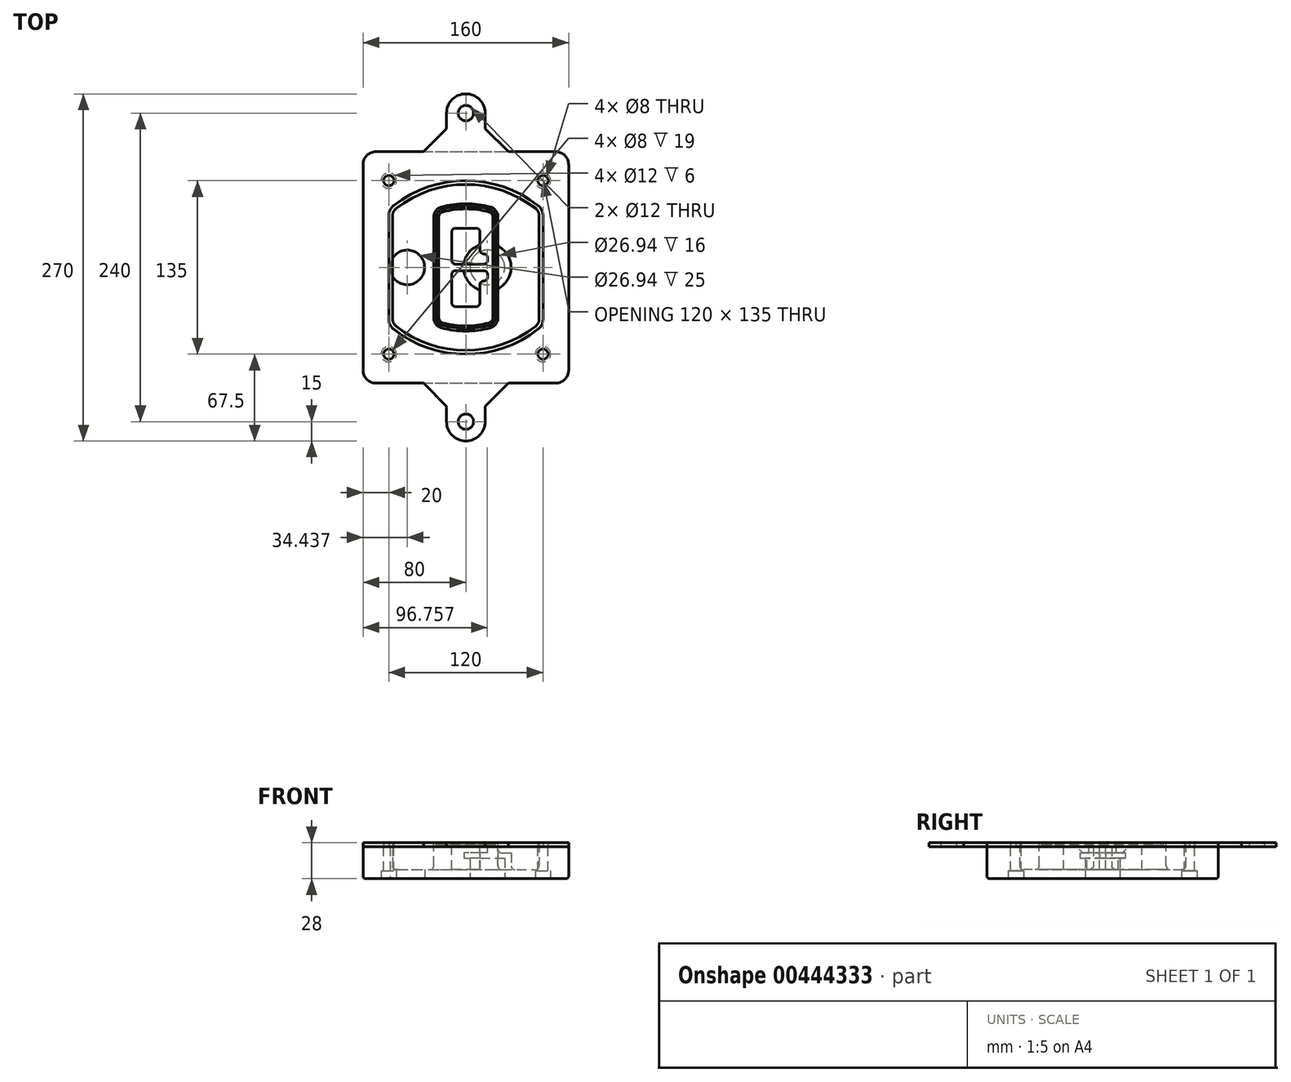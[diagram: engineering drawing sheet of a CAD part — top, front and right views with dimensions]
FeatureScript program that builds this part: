
annotation { "Feature Type Name" : "Feature", "Feature Type Description" : "" }
export const myFeature = defineFeature(function(context is Context, id is Id, definition is map)
    precondition{}
    {
        {
            var Q0;
            Q0=qCreatedBy(makeId("Top.planeOp"),FACE);
            var sketch = newSketch(context, id + "F0", { "sketchPlane" : qUnion([Q0])});
            skPoint(sketch, "E0.rect.middle", {"position": v(0, 0) * mm});
            skLineSegment(sketch, "E1.bottom", {"start": v(-70, -90) * mm, "end": v(70, -90) * mm});
            skLineSegment(sketch, "E1.top", {"start": v(-70, 90) * mm, "end": v(70, 90) * mm});
            skLineSegment(sketch, "E1.left", {"start": v(-80, -80) * mm, "end": v(-80, 80) * mm});
            skLineSegment(sketch, "E1.right", {"start": v(80, -80) * mm, "end": v(80, 80) * mm});
            skLineSegment(sketch, "E2", {"start": v(-80, 90) * mm, "end": v(80, -90) * mm, "construction": true});
            skLineSegment(sketch, "E3", {"start": v(80, 90) * mm, "end": v(-80, -90) * mm, "construction": true});
            skCircle(sketch, "E4", {"center": v(-60, 67.5) * mm, "radius": 4 * mm});
            skCircle(sketch, "E5", {"center": v(60, 67.5) * mm, "radius": 4 * mm});
            skCircle(sketch, "E6", {"center": v(60, -67.5) * mm, "radius": 4 * mm});
            skCircle(sketch, "E7", {"center": v(-60, -67.5) * mm, "radius": 4 * mm});
            skLineSegment(sketch, "E8", {"start": v(-60, 67.5) * mm, "end": v(60, 67.5) * mm, "construction": true});
            skLineSegment(sketch, "E9", {"start": v(60, 67.5) * mm, "end": v(60, -67.5) * mm, "construction": true});
            skLineSegment(sketch, "E10", {"start": v(60, -67.5) * mm, "end": v(-60, -67.5) * mm, "construction": true});
            skLineSegment(sketch, "E11", {"start": v(-60, -67.5) * mm, "end": v(-60, 67.5) * mm, "construction": true});
            skLineSegment(sketch, "E12", {"start": v(-60, 40.3) * mm, "end": v(-60, -40.3) * mm});
            skLineSegment(sketch, "E13", {"start": v(60, 40.3) * mm, "end": v(60, -40.3) * mm});
            skArc(sketch, "E14", {"start": v(56.15, 48.18) * mm, "mid": v(0, 67.5) * mm, "end": v(-56.15, 48.18) * mm});
            skArc(sketch, "E15", {"start": v(-56.15, -48.18) * mm, "mid": v(0, -67.5) * mm, "end": v(56.15, -48.18) * mm});
            skLineSegment(sketch, "E16", {"start": v(-60, 0) * mm, "end": v(60, 0) * mm, "construction": true});
            skPoint(sketch, "E17.visualSharp", {"position": v(-60, -45) * mm});
            skArc(sketch, "E17.filletArc", {"start": v(-60, -40.3) * mm, "mid": v(-58.99, -44.68) * mm, "end": v(-56.15, -48.18) * mm});
            skPoint(sketch, "E18.visualSharp", {"position": v(-60, 45) * mm});
            skArc(sketch, "E18.filletArc", {"start": v(-56.15, 48.18) * mm, "mid": v(-58.99, 44.68) * mm, "end": v(-60, 40.3) * mm});
            skPoint(sketch, "E19.visualSharp", {"position": v(60, 45) * mm});
            skArc(sketch, "E19.filletArc", {"start": v(60, 40.3) * mm, "mid": v(58.99, 44.68) * mm, "end": v(56.15, 48.18) * mm});
            skPoint(sketch, "E20.visualSharp", {"position": v(60, -45) * mm});
            skArc(sketch, "E20.filletArc", {"start": v(56.15, -48.18) * mm, "mid": v(58.99, -44.68) * mm, "end": v(60, -40.3) * mm});
            skPoint(sketch, "E21.visualSharp", {"position": v(-80, 90) * mm});
            skArc(sketch, "E21.filletArc", {"start": v(-70, 90) * mm, "mid": v(-77.07, 87.07) * mm, "end": v(-80, 80) * mm});
            skPoint(sketch, "E22.visualSharp", {"position": v(80, 90) * mm});
            skArc(sketch, "E22.filletArc", {"start": v(80, 80) * mm, "mid": v(77.07, 87.07) * mm, "end": v(70, 90) * mm});
            skPoint(sketch, "E23.visualSharp", {"position": v(80, -90) * mm});
            skArc(sketch, "E23.filletArc", {"start": v(70, -90) * mm, "mid": v(77.07, -87.07) * mm, "end": v(80, -80) * mm});
            skPoint(sketch, "E24.visualSharp", {"position": v(-80, -90) * mm});
            skArc(sketch, "E24.filletArc", {"start": v(-80, -80) * mm, "mid": v(-77.07, -87.07) * mm, "end": v(-70, -90) * mm});
            skArc(sketch, "E25.0", {"start": v(57, 40.3) * mm, "mid": v(56.3, 43.36) * mm, "end": v(54.3, 45.81) * mm});
            skLineSegment(sketch, "E25.1", {"start": v(57, 40.3) * mm, "end": v(57, -40.3) * mm});
            skArc(sketch, "E25.2", {"start": v(54.3, -45.81) * mm, "mid": v(56.3, -43.36) * mm, "end": v(57, -40.3) * mm});
            skArc(sketch, "E25.3", {"start": v(-54.3, -45.81) * mm, "mid": v(0, -64.5) * mm, "end": v(54.3, -45.81) * mm});
            skArc(sketch, "E25.4", {"start": v(-57, -40.3) * mm, "mid": v(-56.3, -43.36) * mm, "end": v(-54.3, -45.81) * mm});
            skArc(sketch, "E25.5", {"start": v(54.3, 45.81) * mm, "mid": v(0, 64.5) * mm, "end": v(-54.3, 45.81) * mm});
            skLineSegment(sketch, "E25.6", {"start": v(-57, 40.3) * mm, "end": v(-57, -40.3) * mm});
            skArc(sketch, "E25.7", {"start": v(-54.3, 45.81) * mm, "mid": v(-56.3, 43.36) * mm, "end": v(-57, 40.3) * mm});
            skArc(sketch, "E26.0", {"start": v(-58.62, 51.33) * mm, "mid": v(-62.58, 46.43) * mm, "end": v(-64, 40.3) * mm});
            skArc(sketch, "E26.1", {"start": v(58.62, 51.33) * mm, "mid": v(0, 71.5) * mm, "end": v(-58.62, 51.33) * mm});
            skArc(sketch, "E26.2", {"start": v(64, 40.3) * mm, "mid": v(62.58, 46.43) * mm, "end": v(58.62, 51.33) * mm});
            skLineSegment(sketch, "E26.3", {"start": v(64, 40.3) * mm, "end": v(64, -40.3) * mm});
            skArc(sketch, "E26.4", {"start": v(58.62, -51.33) * mm, "mid": v(62.58, -46.43) * mm, "end": v(64, -40.3) * mm});
            skLineSegment(sketch, "E26.5", {"start": v(-64, 40.3) * mm, "end": v(-64, -40.3) * mm});
            skArc(sketch, "E26.6", {"start": v(-58.62, -51.33) * mm, "mid": v(0, -71.5) * mm, "end": v(58.62, -51.33) * mm});
            skArc(sketch, "E26.7", {"start": v(-64, -40.3) * mm, "mid": v(-62.58, -46.43) * mm, "end": v(-58.62, -51.33) * mm});
            skSolve(sketch);
        }
        {
            var Q0;
            Q0=makeQuery(id+"F0.imprint","IMPRINT",FACE,{"disambiguationData":[TD([[makeQuery(id+"F0.imprint","IMPRINT",EDGE,{"derivedFrom":sQuery(id+"F0.wireOp",EDGE,"E1.bottom")}),1.0]])]});
            var Q1;
            Q1=makeQuery(id+"F0.imprint","IMPRINT",FACE,{"disambiguationData":[TD([[makeQuery(id+"F0.imprint","IMPRINT",EDGE,{"derivedFrom":sQuery(id+"F0.wireOp",EDGE,"E12")}),1.0]])]});
            var Q2;
            Q2=makeQuery(id+"F0.imprint","IMPRINT",FACE,{"disambiguationData":[TD([[makeQuery(id+"F0.imprint","IMPRINT",EDGE,{"derivedFrom":sQuery(id+"F0.wireOp",EDGE,"E25.0")}),1.0]])]});
            var Q3;
            Q3=makeQuery(id+"F0.imprint","IMPRINT",FACE,{"disambiguationData":[TD([[makeQuery(id+"F0.imprint","IMPRINT",EDGE,{"derivedFrom":sQuery(id+"F0.wireOp",EDGE,"E12")}),-1.0]])]});
            extrude(context, id + "F1", {"entities" : qUnion([Q0, Q1, Q2, Q3]), "oppositeDirection" : true, "depth" : 25 * mm});
        }
        {
            var Q0;
            Q0=makeQuery(id+"F0.imprint","IMPRINT",FACE,{"disambiguationData":[TD([[makeQuery(id+"F0.imprint","IMPRINT",EDGE,{"derivedFrom":sQuery(id+"F0.wireOp",EDGE,"E12")}),1.0]])]});
            extrude(context, id + "F2", {"entities" : qUnion([Q0]), "operationType" : NewBodyOperationType.ADD, "depth" : 3 * mm});
        }
        {
            var Q0;
            Q0=makeQuery(id+"F0.imprint","IMPRINT",FACE,{"disambiguationData":[TD([[makeQuery(id+"F0.imprint","IMPRINT",EDGE,{"derivedFrom":sQuery(id+"F0.wireOp",EDGE,"E25.0")}),1.0]])]});
            extrude(context, id + "F3", {"entities" : qUnion([Q0]), "operationType" : NewBodyOperationType.REMOVE, "oppositeDirection" : true, "depth" : 18 * mm});
        }
        {
            var Q0;
            Q0=makeQuery(id+"F2.opExtrude","CAP_FACE",FACE,{"disambiguationData":[OSD([sQuery(id+"F0.wireOp",EDGE,"E12"),sQuery(id+"F0.wireOp",EDGE,"E13"),sQuery(id+"F0.wireOp",EDGE,"E14"),sQuery(id+"F0.wireOp",EDGE,"E15"),sQuery(id+"F0.wireOp",EDGE,"E17.filletArc"),sQuery(id+"F0.wireOp",EDGE,"E18.filletArc"),sQuery(id+"F0.wireOp",EDGE,"E19.filletArc"),sQuery(id+"F0.wireOp",EDGE,"E20.filletArc"),sQuery(id+"F0.wireOp",EDGE,"E25.0"),sQuery(id+"F0.wireOp",EDGE,"E25.1"),sQuery(id+"F0.wireOp",EDGE,"E25.2"),sQuery(id+"F0.wireOp",EDGE,"E25.3"),sQuery(id+"F0.wireOp",EDGE,"E25.4"),sQuery(id+"F0.wireOp",EDGE,"E25.5"),sQuery(id+"F0.wireOp",EDGE,"E25.6"),sQuery(id+"F0.wireOp",EDGE,"E25.7")])],"isStart":false});
            var sketch = newSketch(context, id + "F4", { "sketchPlane" : qUnion([Q0])});
            skArc(sketch, "E27.0", {"start": v(-19.08, -46.97) * mm, "mid": v(0, -49.5) * mm, "end": v(19.08, -46.97) * mm});
            skArc(sketch, "E28.0", {"start": v(19.08, 46.97) * mm, "mid": v(0, 49.5) * mm, "end": v(-19.08, 46.97) * mm});
            skLineSegment(sketch, "E29", {"start": v(-25, 39.25) * mm, "end": v(-25, -39.25) * mm});
            skLineSegment(sketch, "E30", {"start": v(25, 39.25) * mm, "end": v(25, -39.25) * mm});
            skLineSegment(sketch, "E31", {"start": v(-25, 45.1) * mm, "end": v(25, 45.1) * mm, "construction": true});
            skLineSegment(sketch, "E32", {"start": v(-25, -45.1) * mm, "end": v(25, -45.1) * mm, "construction": true});
            skPoint(sketch, "E33.visualSharp", {"position": v(-25, 45.1) * mm});
            skArc(sketch, "E33.filletArc", {"start": v(-19.08, 46.97) * mm, "mid": v(-23.35, 44.11) * mm, "end": v(-25, 39.25) * mm});
            skPoint(sketch, "E34.visualSharp", {"position": v(25, 45.1) * mm});
            skArc(sketch, "E34.filletArc", {"start": v(25, 39.25) * mm, "mid": v(23.35, 44.11) * mm, "end": v(19.08, 46.97) * mm});
            skPoint(sketch, "E35.visualSharp", {"position": v(25, -45.1) * mm});
            skArc(sketch, "E35.filletArc", {"start": v(19.08, -46.97) * mm, "mid": v(23.35, -44.11) * mm, "end": v(25, -39.25) * mm});
            skPoint(sketch, "E36.visualSharp", {"position": v(-25, -45.1) * mm});
            skArc(sketch, "E36.filletArc", {"start": v(-25, -39.25) * mm, "mid": v(-23.35, -44.11) * mm, "end": v(-19.08, -46.97) * mm});
            skArc(sketch, "E37.0", {"start": v(54.3, 45.81) * mm, "mid": v(0, 64.5) * mm, "end": v(-54.3, 45.81) * mm});
            skArc(sketch, "E37.1", {"start": v(-54.3, 45.81) * mm, "mid": v(-56.3, 43.36) * mm, "end": v(-57, 40.3) * mm});
            skLineSegment(sketch, "E37.2", {"start": v(-57, 40.3) * mm, "end": v(-57, -40.3) * mm});
            skArc(sketch, "E37.3", {"start": v(-57, -40.3) * mm, "mid": v(-56.3, -43.36) * mm, "end": v(-54.3, -45.81) * mm});
            skArc(sketch, "E37.4", {"start": v(-54.3, -45.81) * mm, "mid": v(0, -64.5) * mm, "end": v(54.3, -45.81) * mm});
            skArc(sketch, "E37.5", {"start": v(54.3, -45.81) * mm, "mid": v(56.3, -43.36) * mm, "end": v(57, -40.3) * mm});
            skLineSegment(sketch, "E37.6", {"start": v(57, 40.3) * mm, "end": v(57, -40.3) * mm});
            skArc(sketch, "E37.7", {"start": v(57, 40.3) * mm, "mid": v(56.3, 43.36) * mm, "end": v(54.3, 45.81) * mm});
            skLineSegment(sketch, "E38.0", {"start": v(23, 39.25) * mm, "end": v(23, -39.25) * mm});
            skArc(sketch, "E38.1", {"start": v(18.56, -45.04) * mm, "mid": v(21.76, -42.9) * mm, "end": v(23, -39.25) * mm});
            skArc(sketch, "E38.2", {"start": v(-18.56, -45.04) * mm, "mid": v(0, -47.5) * mm, "end": v(18.56, -45.04) * mm});
            skArc(sketch, "E38.3", {"start": v(-23, -39.25) * mm, "mid": v(-21.76, -42.9) * mm, "end": v(-18.56, -45.04) * mm});
            skLineSegment(sketch, "E38.4", {"start": v(-23, 39.25) * mm, "end": v(-23, -39.25) * mm});
            skArc(sketch, "E38.5", {"start": v(23, 39.25) * mm, "mid": v(21.76, 42.9) * mm, "end": v(18.56, 45.04) * mm});
            skArc(sketch, "E38.6", {"start": v(-18.56, 45.04) * mm, "mid": v(-21.76, 42.9) * mm, "end": v(-23, 39.25) * mm});
            skArc(sketch, "E38.7", {"start": v(18.56, 45.04) * mm, "mid": v(0, 47.5) * mm, "end": v(-18.56, 45.04) * mm});
            skArc(sketch, "E39.0", {"start": v(21, 39.25) * mm, "mid": v(20.18, 41.68) * mm, "end": v(18.04, 43.1) * mm});
            skLineSegment(sketch, "E39.1", {"start": v(21, 39.25) * mm, "end": v(21, -39.25) * mm});
            skArc(sketch, "E39.2", {"start": v(18.04, -43.1) * mm, "mid": v(20.18, -41.68) * mm, "end": v(21, -39.25) * mm});
            skArc(sketch, "E39.3", {"start": v(-18.04, -43.1) * mm, "mid": v(0, -45.5) * mm, "end": v(18.04, -43.1) * mm});
            skArc(sketch, "E39.4", {"start": v(-21, -39.25) * mm, "mid": v(-20.18, -41.68) * mm, "end": v(-18.04, -43.1) * mm});
            skArc(sketch, "E39.5", {"start": v(18.04, 43.1) * mm, "mid": v(0, 45.5) * mm, "end": v(-18.04, 43.1) * mm});
            skLineSegment(sketch, "E39.6", {"start": v(-21, 39.25) * mm, "end": v(-21, -39.25) * mm});
            skArc(sketch, "E39.7", {"start": v(-18.04, 43.1) * mm, "mid": v(-20.18, 41.68) * mm, "end": v(-21, 39.25) * mm});
            skLineSegment(sketch, "E40", {"start": v(-25, 0) * mm, "end": v(25, 0) * mm, "construction": true});
            skLineSegment(sketch, "E41", {"start": v(-11, 5.5) * mm, "end": v(-11, 27.5) * mm});
            skLineSegment(sketch, "E42", {"start": v(-8, 30.5) * mm, "end": v(8, 30.5) * mm});
            skLineSegment(sketch, "E43", {"start": v(11, 27.5) * mm, "end": v(11, 13.5) * mm});
            skLineSegment(sketch, "E44", {"start": v(14, 10.5) * mm, "end": v(14, 10.5) * mm});
            skLineSegment(sketch, "E45", {"start": v(17, 7.5) * mm, "end": v(17, 5.5) * mm});
            skLineSegment(sketch, "E46", {"start": v(14, 2.5) * mm, "end": v(-8, 2.5) * mm});
            skPoint(sketch, "E47.visualSharp", {"position": v(-11, 30.5) * mm});
            skArc(sketch, "E47.filletArc", {"start": v(-8, 30.5) * mm, "mid": v(-10.12, 29.62) * mm, "end": v(-11, 27.5) * mm});
            skPoint(sketch, "E48.visualSharp", {"position": v(11, 30.5) * mm});
            skArc(sketch, "E48.filletArc", {"start": v(11, 27.5) * mm, "mid": v(10.12, 29.62) * mm, "end": v(8, 30.5) * mm});
            skPoint(sketch, "E49.visualSharp", {"position": v(11, 10.5) * mm});
            skArc(sketch, "E49.filletArc", {"start": v(11, 13.5) * mm, "mid": v(11.88, 11.38) * mm, "end": v(14, 10.5) * mm});
            skPoint(sketch, "E50.visualSharp", {"position": v(17, 10.5) * mm});
            skArc(sketch, "E50.filletArc", {"start": v(17, 7.5) * mm, "mid": v(16.12, 9.62) * mm, "end": v(14, 10.5) * mm});
            skPoint(sketch, "E51.visualSharp", {"position": v(17, 2.5) * mm});
            skArc(sketch, "E51.filletArc", {"start": v(14, 2.5) * mm, "mid": v(16.12, 3.38) * mm, "end": v(17, 5.5) * mm});
            skPoint(sketch, "E52.visualSharp", {"position": v(-11, 2.5) * mm});
            skArc(sketch, "E52.filletArc", {"start": v(-11, 5.5) * mm, "mid": v(-10.12, 3.38) * mm, "end": v(-8, 2.5) * mm});
            skLineSegment(sketch, "E53.0.MirrorCS", {"start": v(14, -2.5) * mm, "end": v(-8, -2.5) * mm});
            skArc(sketch, "E54.0.MirrorCS", {"start": v(-11, -5.5) * mm, "mid": v(-10.12, -3.38) * mm, "end": v(-8, -2.5) * mm});
            skLineSegment(sketch, "E55.0.MirrorCS", {"start": v(-11, -5.5) * mm, "end": v(-11, -27.5) * mm});
            skArc(sketch, "E56.0.MirrorCS", {"start": v(-8, -30.5) * mm, "mid": v(-10.12, -29.62) * mm, "end": v(-11, -27.5) * mm});
            skLineSegment(sketch, "E57.0.MirrorCS", {"start": v(-8, -30.5) * mm, "end": v(8, -30.5) * mm});
            skArc(sketch, "E58.0.MirrorCS", {"start": v(11, -27.5) * mm, "mid": v(10.12, -29.62) * mm, "end": v(8, -30.5) * mm});
            skLineSegment(sketch, "E59.0.MirrorCS", {"start": v(11, -27.5) * mm, "end": v(11, -13.5) * mm});
            skArc(sketch, "E60.0.MirrorCS", {"start": v(11, -13.5) * mm, "mid": v(11.88, -11.38) * mm, "end": v(14, -10.5) * mm});
            skArc(sketch, "E61.0.MirrorCS", {"start": v(17, -7.5) * mm, "mid": v(16.12, -9.62) * mm, "end": v(14, -10.5) * mm});
            skLineSegment(sketch, "E62.0.MirrorCS", {"start": v(17, -7.5) * mm, "end": v(17, -5.5) * mm});
            skArc(sketch, "E63.0.MirrorCS", {"start": v(14, -2.5) * mm, "mid": v(16.12, -3.38) * mm, "end": v(17, -5.5) * mm});
            skSolve(sketch);
        }
        {
            var Q0;
            Q0=makeQuery(id+"F4.imprint","IMPRINT",FACE,{"disambiguationData":[TD([[makeQuery(id+"F4.imprint","IMPRINT",EDGE,{"derivedFrom":sQuery(id+"F4.wireOp",EDGE,"E27.0")}),1.0]])]});
            var Q1;
            Q1=makeQuery(id+"F4.imprint","IMPRINT",FACE,{"disambiguationData":[TD([[makeQuery(id+"F4.imprint","IMPRINT",EDGE,{"derivedFrom":sQuery(id+"F4.wireOp",EDGE,"E38.0")}),-1.0]])]});
            var Q2;
            Q2=makeQuery(id+"F4.imprint","IMPRINT",FACE,{"disambiguationData":[TD([[makeQuery(id+"F4.imprint","IMPRINT",EDGE,{"derivedFrom":sQuery(id+"F4.wireOp",EDGE,"E39.0")}),1.0]])]});
            extrude(context, id + "F5", {"entities" : qUnion([Q0, Q1, Q2]), "operationType" : NewBodyOperationType.ADD, "endBound" : BoundingType.UP_TO_NEXT, "oppositeDirection" : true, "depth" : 25 * mm});
        }
        {
            var Q0;
            Q0=makeQuery(id+"F4.imprint","IMPRINT",FACE,{"disambiguationData":[TD([[makeQuery(id+"F4.imprint","IMPRINT",EDGE,{"derivedFrom":sQuery(id+"F4.wireOp",EDGE,"E38.0")}),-1.0]])]});
            extrude(context, id + "F6", {"entities" : qUnion([Q0]), "operationType" : NewBodyOperationType.REMOVE, "oppositeDirection" : true, "depth" : 2 * mm});
        }
        {
            var Q0;
            Q0=makeQuery(id+"F1.opExtrude","CAP_FACE",FACE,{"disambiguationData":[OSD([sQuery(id+"F0.wireOp",EDGE,"E1.bottom"),sQuery(id+"F0.wireOp",EDGE,"E1.top"),sQuery(id+"F0.wireOp",EDGE,"E1.left"),sQuery(id+"F0.wireOp",EDGE,"E1.right"),sQuery(id+"F0.wireOp",EDGE,"E4"),sQuery(id+"F0.wireOp",EDGE,"E5"),sQuery(id+"F0.wireOp",EDGE,"E6"),sQuery(id+"F0.wireOp",EDGE,"E7"),sQuery(id+"F0.wireOp",EDGE,"E21.filletArc"),sQuery(id+"F0.wireOp",EDGE,"E22.filletArc"),sQuery(id+"F0.wireOp",EDGE,"E23.filletArc"),sQuery(id+"F0.wireOp",EDGE,"E24.filletArc")])],"isStart":false});
            var sketch = newSketch(context, id + "F7", { "sketchPlane" : qUnion([Q0])});
            skCircle(sketch, "E64", {"center": v(16.76, 0) * mm, "radius": 13.47 * mm});
            skCircle(sketch, "E65", {"center": v(-45.56, 0) * mm, "radius": 13.47 * mm});
            skLineSegment(sketch, "E66", {"start": v(80, 0) * mm, "end": v(-80, 0) * mm});
            skCircle(sketch, "E67", {"center": v(16.76, 0) * mm, "radius": 18.47 * mm});
            skCircle(sketch, "E68", {"center": v(60, -67.5) * mm, "radius": 6 * mm});
            skCircle(sketch, "E69", {"center": v(-60, -67.5) * mm, "radius": 6 * mm});
            skCircle(sketch, "E70", {"center": v(-60, 67.5) * mm, "radius": 6 * mm});
            skCircle(sketch, "E71", {"center": v(60, 67.5) * mm, "radius": 6 * mm});
            skSolve(sketch);
        }
        {
            var Q0;
            {var subQ1=sQuery(id+"F7.wireOp",EDGE,"E66");var subQ4=sQuery(id+"F7.wireOp",EDGE,"E64");var subQ6=makeQuery(id+"F7.imprint","INTERSECT",VERTEX,{"disambiguationData":[OD(0.0)],"derivedFrom":[subQ4,subQ1]});Q0=makeQuery(id+"F7.imprint","IMPRINT",FACE,{"disambiguationData":[TD([[makeQuery(id+"F7.imprint","IMPRINT",EDGE,{"disambiguationData":[TD([[subQ6,-1.0]])],"derivedFrom":subQ4}),-1.0]])]});}
            var Q1;
            {var subQ0=sQuery(id+"F7.wireOp",EDGE,"E66");var subQ1=sQuery(id+"F7.wireOp",EDGE,"E64");var subQ3=makeQuery(id+"F7.imprint","INTERSECT",VERTEX,{"disambiguationData":[OD(0.0)],"derivedFrom":[subQ1,subQ0]});Q1=makeQuery(id+"F7.imprint","IMPRINT",FACE,{"disambiguationData":[TD([[makeQuery(id+"F7.imprint","IMPRINT",EDGE,{"disambiguationData":[TD([[subQ3,-1.0]])],"derivedFrom":subQ1}),1.0]])]});}
            var Q2;
            {var subQ0=sQuery(id+"F7.wireOp",EDGE,"E66");var subQ1=sQuery(id+"F7.wireOp",EDGE,"E64");var subQ3=makeQuery(id+"F7.imprint","INTERSECT",VERTEX,{"disambiguationData":[OD(0.0)],"derivedFrom":[subQ1,subQ0]});Q2=makeQuery(id+"F7.imprint","IMPRINT",FACE,{"disambiguationData":[TD([[makeQuery(id+"F7.imprint","IMPRINT",EDGE,{"disambiguationData":[TD([[subQ3,1.0]])],"derivedFrom":subQ1}),1.0]])]});}
            var Q3;
            {var subQ1=sQuery(id+"F7.wireOp",EDGE,"E66");var subQ4=sQuery(id+"F7.wireOp",EDGE,"E64");var subQ6=makeQuery(id+"F7.imprint","INTERSECT",VERTEX,{"disambiguationData":[OD(0.0)],"derivedFrom":[subQ4,subQ1]});Q3=makeQuery(id+"F7.imprint","IMPRINT",FACE,{"disambiguationData":[TD([[makeQuery(id+"F7.imprint","IMPRINT",EDGE,{"disambiguationData":[TD([[subQ6,1.0]])],"derivedFrom":subQ4}),-1.0]])]});}
            extrude(context, id + "F8", {"entities" : qUnion([Q0, Q1, Q2, Q3]), "operationType" : NewBodyOperationType.ADD, "oppositeDirection" : true, "depth" : 20 * mm});
        }
        {
            var Q0;
            {var subQ0=sQuery(id+"F7.wireOp",EDGE,"E66");var subQ1=sQuery(id+"F7.wireOp",EDGE,"E64");var subQ3=makeQuery(id+"F7.imprint","INTERSECT",VERTEX,{"disambiguationData":[OD(0.0)],"derivedFrom":[subQ1,subQ0]});Q0=makeQuery(id+"F7.imprint","IMPRINT",FACE,{"disambiguationData":[TD([[makeQuery(id+"F7.imprint","IMPRINT",EDGE,{"disambiguationData":[TD([[subQ3,-1.0]])],"derivedFrom":subQ1}),1.0]])]});}
            var Q1;
            {var subQ0=sQuery(id+"F7.wireOp",EDGE,"E66");var subQ1=sQuery(id+"F7.wireOp",EDGE,"E64");var subQ3=makeQuery(id+"F7.imprint","INTERSECT",VERTEX,{"disambiguationData":[OD(0.0)],"derivedFrom":[subQ1,subQ0]});Q1=makeQuery(id+"F7.imprint","IMPRINT",FACE,{"disambiguationData":[TD([[makeQuery(id+"F7.imprint","IMPRINT",EDGE,{"disambiguationData":[TD([[subQ3,1.0]])],"derivedFrom":subQ1}),1.0]])]});}
            extrude(context, id + "F9", {"entities" : qUnion([Q0, Q1]), "operationType" : NewBodyOperationType.REMOVE, "oppositeDirection" : true, "depth" : 16 * mm});
        }
        {
            var Q0;
            {var subQ0=sQuery(id+"F7.wireOp",EDGE,"E66");var subQ1=sQuery(id+"F7.wireOp",EDGE,"E65");var subQ3=makeQuery(id+"F7.imprint","INTERSECT",VERTEX,{"disambiguationData":[OD(0.0)],"derivedFrom":[subQ1,subQ0]});Q0=makeQuery(id+"F7.imprint","IMPRINT",FACE,{"disambiguationData":[TD([[makeQuery(id+"F7.imprint","IMPRINT",EDGE,{"disambiguationData":[TD([[subQ3,-1.0]])],"derivedFrom":subQ1}),1.0]])]});}
            var Q1;
            {var subQ0=sQuery(id+"F7.wireOp",EDGE,"E66");var subQ1=sQuery(id+"F7.wireOp",EDGE,"E65");var subQ3=makeQuery(id+"F7.imprint","INTERSECT",VERTEX,{"disambiguationData":[OD(0.0)],"derivedFrom":[subQ1,subQ0]});Q1=makeQuery(id+"F7.imprint","IMPRINT",FACE,{"disambiguationData":[TD([[makeQuery(id+"F7.imprint","IMPRINT",EDGE,{"disambiguationData":[TD([[subQ3,1.0]])],"derivedFrom":subQ1}),1.0]])]});}
            extrude(context, id + "F10", {"entities" : qUnion([Q0, Q1]), "operationType" : NewBodyOperationType.REMOVE, "oppositeDirection" : true, "depth" : 25 * mm});
        }
        {
            var Q0;
            Q0=makeQuery(id+"F7.imprint","IMPRINT",FACE,{"disambiguationData":[TD([[makeQuery(id+"F7.imprint","IMPRINT",EDGE,{"derivedFrom":sQuery(id+"F7.wireOp",EDGE,"E68")}),1.0]])]});
            var Q1;
            Q1=makeQuery(id+"F7.imprint","IMPRINT",FACE,{"disambiguationData":[TD([[makeQuery(id+"F7.imprint","IMPRINT",EDGE,{"derivedFrom":makeQuery(id+"F1.opExtrude","CAP_EDGE",EDGE,{"disambiguationData":[OSD([sQuery(id+"F0.wireOp",EDGE,"E5")])],"isStart":false})}),-1.0]])]});
            var Q2;
            Q2=makeQuery(id+"F7.imprint","IMPRINT",FACE,{"disambiguationData":[TD([[makeQuery(id+"F7.imprint","IMPRINT",EDGE,{"derivedFrom":sQuery(id+"F7.wireOp",EDGE,"E69")}),1.0]])]});
            var Q3;
            Q3=makeQuery(id+"F7.imprint","IMPRINT",FACE,{"disambiguationData":[TD([[makeQuery(id+"F7.imprint","IMPRINT",EDGE,{"derivedFrom":makeQuery(id+"F1.opExtrude","CAP_EDGE",EDGE,{"disambiguationData":[OSD([sQuery(id+"F0.wireOp",EDGE,"E4")])],"isStart":false})}),-1.0]])]});
            var Q4;
            Q4=makeQuery(id+"F7.imprint","IMPRINT",FACE,{"disambiguationData":[TD([[makeQuery(id+"F7.imprint","IMPRINT",EDGE,{"derivedFrom":sQuery(id+"F7.wireOp",EDGE,"E70")}),1.0]])]});
            var Q5;
            Q5=makeQuery(id+"F7.imprint","IMPRINT",FACE,{"disambiguationData":[TD([[makeQuery(id+"F7.imprint","IMPRINT",EDGE,{"derivedFrom":makeQuery(id+"F1.opExtrude","CAP_EDGE",EDGE,{"disambiguationData":[OSD([sQuery(id+"F0.wireOp",EDGE,"E7")])],"isStart":false})}),-1.0]])]});
            var Q6;
            Q6=makeQuery(id+"F7.imprint","IMPRINT",FACE,{"disambiguationData":[TD([[makeQuery(id+"F7.imprint","IMPRINT",EDGE,{"derivedFrom":sQuery(id+"F7.wireOp",EDGE,"E71")}),1.0]])]});
            var Q7;
            Q7=makeQuery(id+"F7.imprint","IMPRINT",FACE,{"disambiguationData":[TD([[makeQuery(id+"F7.imprint","IMPRINT",EDGE,{"derivedFrom":makeQuery(id+"F1.opExtrude","CAP_EDGE",EDGE,{"disambiguationData":[OSD([sQuery(id+"F0.wireOp",EDGE,"E6")])],"isStart":false})}),-1.0]])]});
            extrude(context, id + "F11", {"entities" : qUnion([Q0, Q1, Q2, Q3, Q4, Q5, Q6, Q7]), "operationType" : NewBodyOperationType.REMOVE, "oppositeDirection" : true, "depth" : 6 * mm});
        }
        {
            var Q0;
            Q0=makeQuery(id+"F9.boolean.opBoolean","COPY",FACE,{"derivedFrom":makeQuery(id+"F9.opExtrude","CAP_FACE",FACE,{"disambiguationData":[OSD([sQuery(id+"F7.wireOp",EDGE,"E64")])],"isStart":false})});
            var sketch = newSketch(context, id + "F12", { "sketchPlane" : qUnion([Q0])});
            skArc(sketch, "E72.0", {"start": v(11, 17.55) * mm, "mid": v(2.57, 11.82) * mm, "end": v(-1.54, 2.5) * mm});
            skArc(sketch, "E72.1", {"start": v(-1.54, -2.5) * mm, "mid": v(2.57, -11.82) * mm, "end": v(11, -17.55) * mm});
            skLineSegment(sketch, "E73", {"start": v(-1.54, -2.5) * mm, "end": v(14, -2.5) * mm});
            skLineSegment(sketch, "E74.0", {"start": v(14, 2.5) * mm, "end": v(-1.54, 2.5) * mm});
            skArc(sketch, "E74.1", {"start": v(14, 2.5) * mm, "mid": v(16.12, 3.38) * mm, "end": v(17, 5.5) * mm});
            skLineSegment(sketch, "E74.2", {"start": v(17, 7.5) * mm, "end": v(17, 5.5) * mm});
            skArc(sketch, "E74.3", {"start": v(17, 7.5) * mm, "mid": v(16.12, 9.62) * mm, "end": v(14, 10.5) * mm});
            skArc(sketch, "E74.4", {"start": v(11, 13.5) * mm, "mid": v(11.88, 11.38) * mm, "end": v(14, 10.5) * mm});
            skLineSegment(sketch, "E74.5", {"start": v(11, 17.55) * mm, "end": v(11, 13.5) * mm});
            skLineSegment(sketch, "E74.7", {"start": v(14, -2.5) * mm, "end": v(-1.54, -2.5) * mm});
            skArc(sketch, "E74.8", {"start": v(14, -2.5) * mm, "mid": v(16.12, -3.38) * mm, "end": v(17, -5.5) * mm});
            skLineSegment(sketch, "E74.9", {"start": v(17, -7.5) * mm, "end": v(17, -5.5) * mm});
            skArc(sketch, "E74.10", {"start": v(17, -7.5) * mm, "mid": v(16.12, -9.62) * mm, "end": v(14, -10.5) * mm});
            skArc(sketch, "E74.11", {"start": v(11, -13.5) * mm, "mid": v(11.88, -11.38) * mm, "end": v(14, -10.5) * mm});
            skLineSegment(sketch, "E74.12", {"start": v(11, -17.55) * mm, "end": v(11, -13.5) * mm});
            skPoint(sketch, "E75.orphan", {"position": v(11, -27.5) * mm});
            skPoint(sketch, "E76.orphan", {"position": v(-8, -2.5) * mm});
            skPoint(sketch, "E77.orphan", {"position": v(-8, 2.5) * mm});
            skPoint(sketch, "E78.orphan", {"position": v(11, 27.5) * mm});
            skSolve(sketch);
        }
        {
            var Q0;
            {var subQ7=sQuery(id+"F12.wireOp",EDGE,"E72.0");var subQ14=sQuery(id+"F12.wireOp",EDGE,"E72.1");var subQ16=sQuery(id+"F12.wireOp",EDGE,"E74.1");var subQ18=sQuery(id+"F12.wireOp",EDGE,"E74.8");Q0=qUnion([makeQuery(id+"F12.imprint","IMPRINT",FACE,{"disambiguationData":[TD([[makeQuery(id+"F12.imprint","IMPRINT",EDGE,{"derivedFrom":subQ7}),1.0]])]}),makeQuery(id+"F12.imprint","IMPRINT",FACE,{"disambiguationData":[TD([[makeQuery(id+"F12.imprint","IMPRINT",EDGE,{"derivedFrom":subQ14}),1.0]])]}),makeQuery(id+"F12.imprint","IMPRINT",FACE,{"disambiguationData":[TD([[makeQuery(id+"F12.imprint","IMPRINT",EDGE,{"derivedFrom":subQ16}),1.0]])]}),makeQuery(id+"F12.imprint","IMPRINT",FACE,{"disambiguationData":[TD([[makeQuery(id+"F12.imprint","IMPRINT",EDGE,{"derivedFrom":subQ18}),-1.0]])]})]);}
            var Q1;
            Q1=makeQuery(id+"F5.boolean.opBoolean","SPLIT",FACE,{"disambiguationData":[TD([makeQuery(id+"F5.opExtrude","SWEPT_FACE",FACE,{"disambiguationData":[OSD([sQuery(id+"F4.wireOp",EDGE,"E41")])]})])],"derivedFrom":makeQuery(id+"F3.boolean.opBoolean","COPY",FACE,{"derivedFrom":makeQuery(id+"F3.opExtrude","CAP_FACE",FACE,{"disambiguationData":[OSD([sQuery(id+"F0.wireOp",EDGE,"E25.0"),sQuery(id+"F0.wireOp",EDGE,"E25.1"),sQuery(id+"F0.wireOp",EDGE,"E25.2"),sQuery(id+"F0.wireOp",EDGE,"E25.3"),sQuery(id+"F0.wireOp",EDGE,"E25.4"),sQuery(id+"F0.wireOp",EDGE,"E25.5"),sQuery(id+"F0.wireOp",EDGE,"E25.6"),sQuery(id+"F0.wireOp",EDGE,"E25.7")])],"isStart":false})})});
            extrude(context, id + "F13", {"entities" : qUnion([Q0]), "operationType" : NewBodyOperationType.REMOVE, "endBound" : BoundingType.UP_TO_SURFACE, "endBoundEntityFace" : qUnion([Q1]), "depth" : 25 * mm});
        }
        {
            var Q0;
            Q0=makeQuery(id+"F3.boolean.opBoolean","COPY",EDGE,{"derivedFrom":makeQuery(id+"F3.opExtrude","CAP_EDGE",EDGE,{"disambiguationData":[OSD([sQuery(id+"F0.wireOp",EDGE,"E25.6")])],"isStart":false})});
            var Q1;
            Q1=makeQuery(id+"F8.boolean.opBoolean","INTERSECT",EDGE,{"derivedFrom":[makeQuery(id+"F5.opExtrude","SWEPT_FACE",FACE,{"disambiguationData":[OSD([sQuery(id+"F4.wireOp",EDGE,"E30")])]}),makeQuery(id+"F8.opExtrude","CAP_FACE",FACE,{"disambiguationData":[OSD([sQuery(id+"F7.wireOp",EDGE,"E67")])],"isStart":false})]});
            var Q2;
            Q2=makeQuery(id+"F8.boolean.opBoolean","INTERSECT",EDGE,{"disambiguationData":[OD(1.0)],"derivedFrom":[makeQuery(id+"F5.opExtrude","SWEPT_FACE",FACE,{"disambiguationData":[OSD([sQuery(id+"F4.wireOp",EDGE,"E30")])]}),makeQuery(id+"F8.opExtrude","SWEPT_FACE",FACE,{"disambiguationData":[OSD([sQuery(id+"F7.wireOp",EDGE,"E67")])]})]});
            var Q3;
            {var subQ0=sQuery(id+"F4.wireOp",EDGE,"E30");Q3=makeQuery(id+"F8.boolean.opBoolean","SPLIT",EDGE,{"disambiguationData":[TD([makeQuery(id+"F5.opExtrude","SWEPT_FACE",FACE,{"disambiguationData":[OSD([sQuery(id+"F4.wireOp",EDGE,"E35.filletArc")])]})])],"derivedFrom":makeQuery(id+"F5.opExtrude","CAP_EDGE",EDGE,{"disambiguationData":[OSD([subQ0])],"isStart":false})});}
            var Q4;
            {var subQ0=sQuery(id+"F0.wireOp",EDGE,"E25.7");var subQ1=sQuery(id+"F0.wireOp",EDGE,"E25.1");var subQ2=sQuery(id+"F0.wireOp",EDGE,"E25.6");var subQ3=sQuery(id+"F0.wireOp",EDGE,"E25.5");var subQ4=sQuery(id+"F0.wireOp",EDGE,"E25.4");var subQ5=sQuery(id+"F0.wireOp",EDGE,"E25.0");var subQ6=sQuery(id+"F0.wireOp",EDGE,"E25.2");var subQ7=sQuery(id+"F0.wireOp",EDGE,"E25.3");Q4=makeQuery(id+"F8.boolean.opBoolean","INTERSECT",EDGE,{"derivedFrom":[makeQuery(id+"F5.boolean.opBoolean","SPLIT",FACE,{"disambiguationData":[TD([makeQuery(id+"F2.opExtrude","SWEPT_FACE",FACE,{"disambiguationData":[OSD([subQ5])]})])],"derivedFrom":makeQuery(id+"F3.boolean.opBoolean","COPY",FACE,{"derivedFrom":makeQuery(id+"F3.opExtrude","CAP_FACE",FACE,{"disambiguationData":[OSD([subQ5,subQ1,subQ6,subQ7,subQ4,subQ3,subQ2,subQ0])],"isStart":false})})}),makeQuery(id+"F8.opExtrude","SWEPT_FACE",FACE,{"disambiguationData":[OSD([sQuery(id+"F7.wireOp",EDGE,"E67")])]})]});}
            var Q5;
            Q5=makeQuery(id+"F8.boolean.opBoolean","INTERSECT",EDGE,{"disambiguationData":[OD(0.0)],"derivedFrom":[makeQuery(id+"F5.opExtrude","SWEPT_FACE",FACE,{"disambiguationData":[OSD([sQuery(id+"F4.wireOp",EDGE,"E30")])]}),makeQuery(id+"F8.opExtrude","SWEPT_FACE",FACE,{"disambiguationData":[OSD([sQuery(id+"F7.wireOp",EDGE,"E67")])]})]});
            fillet(context, id + "F14", {"entities" : qUnion([Q0, Q1, Q2, Q3, Q4, Q5]), "radius" : 3 * mm, "tangentPropagation" : true, "allowEdgeOverflow" : false});
        }
        {
            var Q0;
            {var subQ0=sQuery(id+"F0.wireOp",EDGE,"E21.filletArc");var subQ1=sQuery(id+"F0.wireOp",EDGE,"E7");var subQ2=sQuery(id+"F0.wireOp",EDGE,"E6");var subQ3=sQuery(id+"F0.wireOp",EDGE,"E5");var subQ4=sQuery(id+"F0.wireOp",EDGE,"E4");var subQ5=sQuery(id+"F0.wireOp",EDGE,"E22.filletArc");var subQ6=sQuery(id+"F0.wireOp",EDGE,"E1.bottom");var subQ7=sQuery(id+"F0.wireOp",EDGE,"E1.right");var subQ8=sQuery(id+"F0.wireOp",EDGE,"E1.top");var subQ9=sQuery(id+"F0.wireOp",EDGE,"E1.left");var subQ10=sQuery(id+"F0.wireOp",EDGE,"E23.filletArc");var subQ11=sQuery(id+"F0.wireOp",EDGE,"E24.filletArc");Q0=makeQuery(id+"F2.boolean.opBoolean","SPLIT",FACE,{"disambiguationData":[TD([makeQuery(id+"F1.opExtrude","SWEPT_FACE",FACE,{"disambiguationData":[OSD([subQ6])]})])],"derivedFrom":makeQuery(id+"F1.opExtrude","CAP_FACE",FACE,{"disambiguationData":[OSD([subQ6,subQ8,subQ9,subQ7,subQ4,subQ3,subQ2,subQ1,subQ0,subQ5,subQ10,subQ11])],"isStart":true})});}
            var sketch = newSketch(context, id + "F15", { "sketchPlane" : qUnion([Q0])});
            skLineSegment(sketch, "E79", {"start": v(0, 90) * mm, "end": v(0, 120) * mm, "construction": true});
            skCircle(sketch, "E80", {"center": v(0, 120) * mm, "radius": 6 * mm});
            skArc(sketch, "E81", {"start": v(15, 120) * mm, "mid": v(0, 135) * mm, "end": v(-15, 120) * mm});
            skLineSegment(sketch, "E82", {"start": v(15, 120) * mm, "end": v(15, 108) * mm});
            skLineSegment(sketch, "E83", {"start": v(15, 108) * mm, "end": v(33, 90) * mm});
            skLineSegment(sketch, "E84", {"start": v(-15, 120) * mm, "end": v(-15, 108) * mm});
            skLineSegment(sketch, "E85", {"start": v(-15, 108) * mm, "end": v(-33, 90) * mm});
            skLineSegment(sketch, "E86", {"start": v(-80, 0) * mm, "end": v(80, 0) * mm, "construction": true});
            skArc(sketch, "E87.MirrorCS", {"start": v(-15, 120) * mm, "mid": v(0, 135) * mm, "end": v(15, 120) * mm});
            skArc(sketch, "E88.MirrorCS", {"start": v(-15, -120) * mm, "mid": v(0, -135) * mm, "end": v(15, -120) * mm});
            skLineSegment(sketch, "E89.MirrorCS", {"start": v(15, -120) * mm, "end": v(15, -108) * mm});
            skArc(sketch, "E90.MirrorCS", {"start": v(15, -120) * mm, "mid": v(0, -135) * mm, "end": v(-15, -120) * mm});
            skLineSegment(sketch, "E91.MirrorCS", {"start": v(-15, -108) * mm, "end": v(-33, -90) * mm});
            skLineSegment(sketch, "E92.MirrorCS", {"start": v(-15, -120) * mm, "end": v(-15, -108) * mm});
            skLineSegment(sketch, "E93.MirrorCS", {"start": v(15, -108) * mm, "end": v(33, -90) * mm});
            skCircle(sketch, "E94.MirrorC", {"center": v(0, -120) * mm, "radius": 6 * mm});
            skLineSegment(sketch, "E95.MirrorCS", {"start": v(0, -90) * mm, "end": v(0, -120) * mm, "construction": true});
            skSolve(sketch);
        }
        {
            var Q0;
            Q0=makeQuery(id+"F15.imprint","IMPRINT",FACE,{"disambiguationData":[TD([[makeQuery(id+"F15.imprint","IMPRINT",EDGE,{"derivedFrom":sQuery(id+"F15.wireOp",EDGE,"E84")}),1.0]])]});
            var Q1;
            Q1=makeQuery(id+"F15.imprint","IMPRINT",FACE,{"disambiguationData":[TD([[makeQuery(id+"F15.imprint","IMPRINT",EDGE,{"derivedFrom":makeQuery(id+"F1.opExtrude","CAP_EDGE",EDGE,{"disambiguationData":[OSD([sQuery(id+"F0.wireOp",EDGE,"E1.left")])],"isStart":true})}),-1.0]])]});
            var Q2;
            {var subQ0=sQuery(id+"F15.wireOp",EDGE,"E91.MirrorCS");Q2=makeQuery(id+"F15.imprint","IMPRINT",FACE,{"disambiguationData":[TD([[makeQuery(id+"F15.imprint","IMPRINT",EDGE,{"derivedFrom":subQ0}),-1.0]])]});}
            var Q3;
            Q3=makeQuery(id+"F2.opExtrude","CAP_FACE",FACE,{"disambiguationData":[OSD([sQuery(id+"F0.wireOp",EDGE,"E12"),sQuery(id+"F0.wireOp",EDGE,"E13"),sQuery(id+"F0.wireOp",EDGE,"E14"),sQuery(id+"F0.wireOp",EDGE,"E15"),sQuery(id+"F0.wireOp",EDGE,"E17.filletArc"),sQuery(id+"F0.wireOp",EDGE,"E18.filletArc"),sQuery(id+"F0.wireOp",EDGE,"E19.filletArc"),sQuery(id+"F0.wireOp",EDGE,"E20.filletArc"),sQuery(id+"F0.wireOp",EDGE,"E25.0"),sQuery(id+"F0.wireOp",EDGE,"E25.1"),sQuery(id+"F0.wireOp",EDGE,"E25.2"),sQuery(id+"F0.wireOp",EDGE,"E25.3"),sQuery(id+"F0.wireOp",EDGE,"E25.4"),sQuery(id+"F0.wireOp",EDGE,"E25.5"),sQuery(id+"F0.wireOp",EDGE,"E25.6"),sQuery(id+"F0.wireOp",EDGE,"E25.7")])],"isStart":false});
            extrude(context, id + "F16", {"entities" : qUnion([Q0, Q1, Q2]), "endBound" : BoundingType.UP_TO_SURFACE, "endBoundEntityFace" : qUnion([Q3]), "depth" : 25 * mm});
        }
        {
            var Q0;
            Q0=makeQuery(id+"F1.opExtrude","CAP_EDGE",EDGE,{"disambiguationData":[OSD([sQuery(id+"F0.wireOp",EDGE,"E1.bottom")])],"isStart":false});
            fillet(context, id + "F17", {"entities" : qUnion([Q0]), "radius" : 2 * mm, "tangentPropagation" : true, "allowEdgeOverflow" : false});
        }
    });
